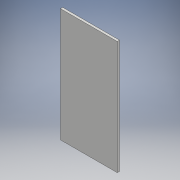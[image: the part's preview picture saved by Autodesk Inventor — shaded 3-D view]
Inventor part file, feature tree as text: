
AUTODESK INVENTOR PART (.ipt)
format: ipt  version: 2018 (Build 220112000, 112)  size: 92,160 bytes
history: native  units: mm
features: sketch x2, extrude x1
ambient origin geometry x8: Origin, YZ Plane, XZ Plane, XY Plane, X Axis, Y Axis, Z Axis, Center Point
bodies: 实体1 (feature_tree)
feature tree (3):
  extrude  "拉伸1"  Depth=50.0mm
  sketch  "草图2"  dims[d2=1.0mm d3=0.0mm]
  sketch  "草图1"  dims[d0=25.0mm d1=50.0mm]
